# Revit family: m8crebf_rendering_asm.iam (m8crebf_rendering_asm_Simplify_3)
name_source: partatom
category: Generic Models
units: mm (PartAtom-declared; Revit-internal decimal feet)

## family parameters
Always vertical = Yes
Can host rebar = No
Cut with Voids When Loaded = No
Maintain Annotation Orientation = No
Part Type = Normal
Room Calculation Point = No
Round Connector Dimension = Use Diameter
Shared = No
Work Plane-Based = No

## types (1)
- Standard
    Connector_2_Diameter = 0' - 0 1/4"
    Connector_3_Diameter = 0' - 0 1/4"
    Connector_4_Diameter = 0' - 1 1/4"
    Connector_5_Diameter = 0' - 1 1/4"
    Default Elevation = 0' - 0"
    Description = BI-LEVEL RADII FOUNTAIN W/ INTEGRATED ELECTRONIC BOTTLE FILLER, REFRIGERATED
    Design State = 1
    Manufacturer = Oasis International
    Model = M8CREBF
    Part Number = M8WREBF_ASM
    Preprocessor = CREO PARAMETRIC BY PTC INC, 2022281
    Revision Number = 46LAST_VERSION
    Sending System = CREO PARAMETRIC BY PTC INC, 2022281
    Title = M8WREBF_ASM
    URL = https://www.oasiscoolers.com

## geometry (parser evidence)
native form markers: Sweep x3
no freeform markers — native parametric forms only
